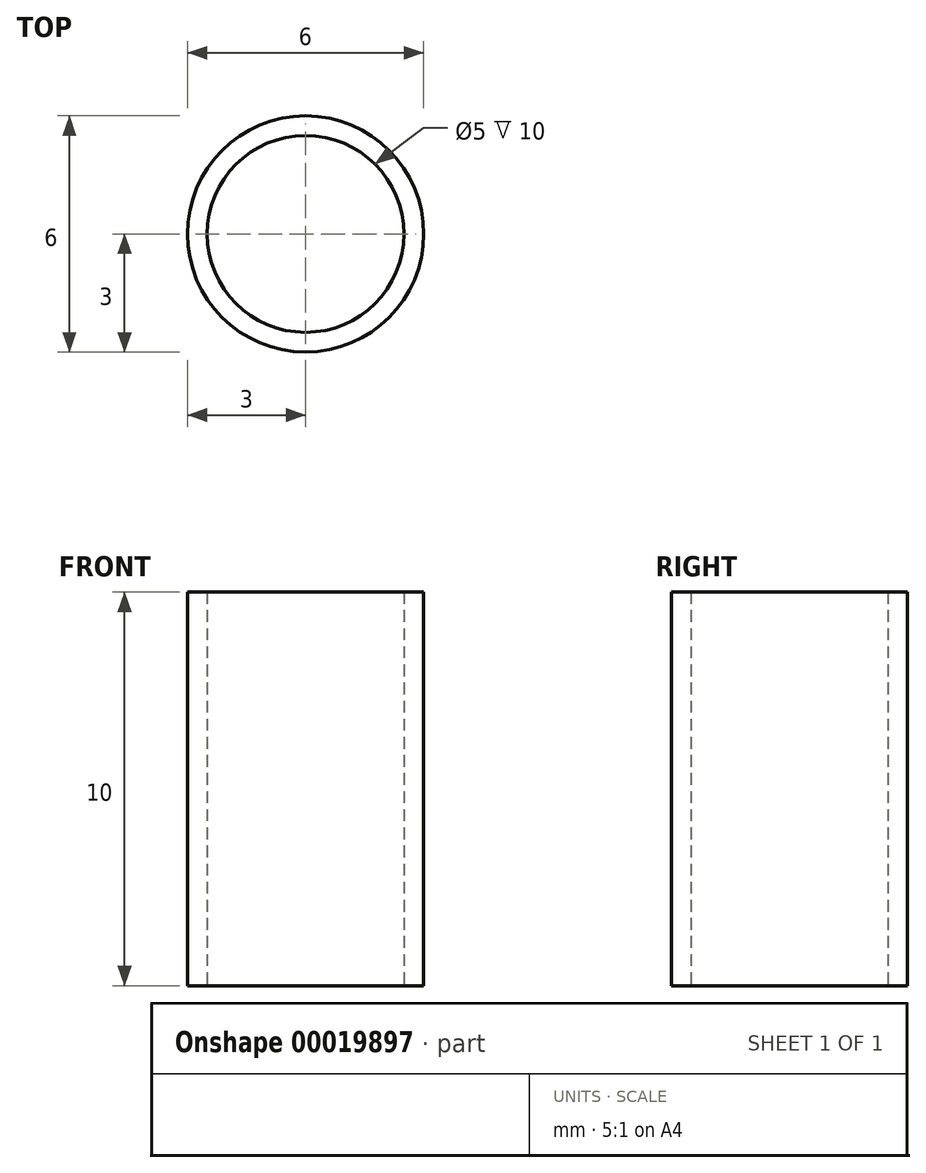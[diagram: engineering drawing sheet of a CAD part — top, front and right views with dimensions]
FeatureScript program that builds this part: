
annotation { "Feature Type Name" : "Feature", "Feature Type Description" : "" }
export const myFeature = defineFeature(function(context is Context, id is Id, definition is map)
    precondition{}
    {
        {
            var Q0;
            Q0=qCreatedBy(makeId("Top.planeOp"),FACE);
            var sketch = newSketch(context, id + "F0", { "sketchPlane" : qUnion([Q0])});
            skCircle(sketch, "E0", {"center": v(0, 0) * mm, "radius": 2.5 * mm});
            skCircle(sketch, "E1", {"center": v(0, 0) * mm, "radius": 3 * mm});
            skSolve(sketch);
        }
        {
            var Q0;
            Q0=makeQuery(id+"F0.imprint","IMPRINT",FACE,{"disambiguationData":[TD([[makeQuery(id+"F0.imprint","IMPRINT",EDGE,{"derivedFrom":sQuery(id+"F0.wireOp",EDGE,"E0")}),-1.0]])]});
            extrude(context, id + "F1", {"entities" : qUnion([Q0]), "depth" : 10 * mm});
        }
    });
